# Revit family: Window_Finlandia_Sauna-Window-Opening
name_source: partatom
category: Windows
units: mm (PartAtom-declared; Revit-internal decimal feet)

## family parameters
Classification Number = 23.30.20.17.11
Cut with Voids When Loaded = No
Host = Face
Room Calculation Point = No
Shared = Yes

## types (1)
- Window_Finlandia_Sauna-Window-Opening
    Assembly Code = B2020130
    Construction Details = http://www.arcat.com
    Default Elevation = 0' - 0"
    Description = Finlandia Fixed Window Opening - Size as Specified
    Expected Lifespan (Years) = 0
    Green Building-LEED = http://www.arcat.com
    Keynote = 13052
    Maintenance Schedule (Months) = 0
    Manufacturer = Finlandia Sauna Products, Inc.
    Manufacturer Fax = 503-684-1120
    Manufacturer Website = http://www.finlandiasauna.com
    Model = As Specified
    Product Data = http://www.arcat.com
    Revision = R1_2014-07
    Sales Information = http://www.finlandiasauna.com
    Send Message = http://www.arcat.com
    Specification = http://www.arcat.com
    URL = http://www.finlandiasauna.com
    Warranty Duration (Years) = 0

## geometry (parser evidence)
native form markers: Sweep x2
no freeform markers — native parametric forms only
